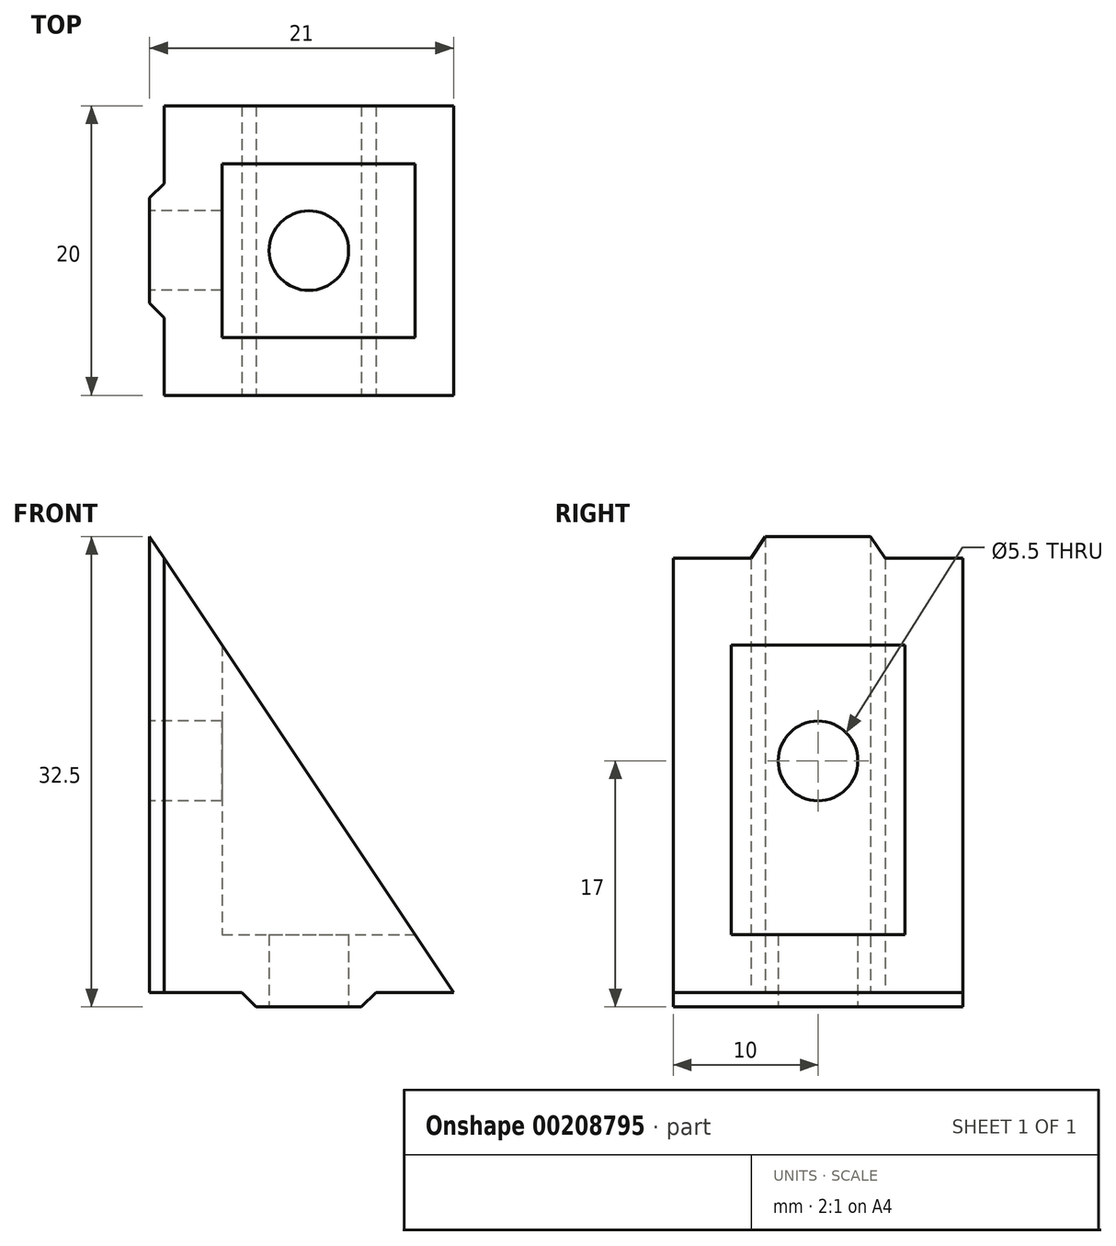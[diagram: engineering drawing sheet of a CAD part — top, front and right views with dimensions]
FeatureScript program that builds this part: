
annotation { "Feature Type Name" : "Feature", "Feature Type Description" : "" }
export const myFeature = defineFeature(function(context is Context, id is Id, definition is map)
    precondition{}
    {
        {
            var Q0;
            Q0=qCreatedBy(makeId("Top.planeOp"),FACE);
            var sketch = newSketch(context, id + "F0", { "sketchPlane" : qUnion([Q0])});
            skLineSegment(sketch, "E0.bottom", {"start": v(-20, 20) * mm, "end": v(0, 20) * mm});
            skLineSegment(sketch, "E0.top", {"start": v(-20, 0) * mm, "end": v(0, 0) * mm});
            skLineSegment(sketch, "E0.left", {"start": v(-20, 20) * mm, "end": v(-20, 0) * mm});
            skLineSegment(sketch, "E0.right", {"start": v(0, 20) * mm, "end": v(0, 0) * mm});
            skSolve(sketch);
        }
        {
            var Q0;
            Q0=makeQuery(id+"F0.imprint","IMPRINT",FACE,{"disambiguationData":[TD([[makeQuery(id+"F0.imprint","IMPRINT",EDGE,{"derivedFrom":sQuery(id+"F0.wireOp",EDGE,"E0.bottom")}),-1.0]])]});
            extrude(context, id + "F1", {"entities" : qUnion([Q0]), "depth" : 4 * mm});
        }
        {
            var Q0;
            Q0=makeQuery(id+"F1.opExtrude","CAP_FACE",FACE,{"disambiguationData":[OSD([sQuery(id+"F0.wireOp",EDGE,"E0.bottom"),sQuery(id+"F0.wireOp",EDGE,"E0.top"),sQuery(id+"F0.wireOp",EDGE,"E0.left"),sQuery(id+"F0.wireOp",EDGE,"E0.right")])],"isStart":false});
            var sketch = newSketch(context, id + "F2", { "sketchPlane" : qUnion([Q0])});
            skLineSegment(sketch, "E1", {"start": v(0, 0) * mm, "end": v(-20, 0) * mm});
            skLineSegment(sketch, "E2", {"start": v(-20, 0) * mm, "end": v(-20, 20) * mm});
            skLineSegment(sketch, "E3", {"start": v(-20, 20) * mm, "end": v(0, 20) * mm});
            skLineSegment(sketch, "E4", {"start": v(0, 20) * mm, "end": v(0, 16) * mm});
            skLineSegment(sketch, "E5", {"start": v(0, 16) * mm, "end": v(-16, 16) * mm});
            skLineSegment(sketch, "E6", {"start": v(-16, 16) * mm, "end": v(-16, 4) * mm});
            skLineSegment(sketch, "E7", {"start": v(-16, 4) * mm, "end": v(0, 4) * mm});
            skLineSegment(sketch, "E8", {"start": v(0, 4) * mm, "end": v(0, 0) * mm});
            skSolve(sketch);
        }
        {
            var Q0;
            Q0=makeQuery(id+"F2.imprint","IMPRINT",FACE,{"disambiguationData":[TD([[makeQuery(id+"F2.imprint","IMPRINT",EDGE,{"derivedFrom":sQuery(id+"F2.wireOp",EDGE,"E1")}),1.0]])]});
            extrude(context, id + "F3", {"entities" : qUnion([Q0]), "operationType" : NewBodyOperationType.ADD, "depth" : 26 * mm});
        }
        {
            var Q0;
            Q0=makeQuery(id+"F3.boolean.opBoolean","MERGE",FACE,{"derivedFrom":[makeQuery(id+"F1.opExtrude","SWEPT_FACE",FACE,{"disambiguationData":[OSD([sQuery(id+"F0.wireOp",EDGE,"E0.top")])]}),makeQuery(id+"F3.opExtrude","SWEPT_FACE",FACE,{"disambiguationData":[OSD([sQuery(id+"F2.wireOp",EDGE,"E1")])]})]});
            var sketch = newSketch(context, id + "F4", { "sketchPlane" : qUnion([Q0])});
            skLineSegment(sketch, "E9", {"start": v(-20, 30) * mm, "end": v(0, 30) * mm});
            skLineSegment(sketch, "E10", {"start": v(0, 30) * mm, "end": v(0, 0) * mm});
            skLineSegment(sketch, "E11", {"start": v(0, 0) * mm, "end": v(-20, 30) * mm});
            skSolve(sketch);
        }
        {
            var Q0;
            Q0=makeQuery(id+"F4.imprint","IMPRINT",FACE,{"disambiguationData":[TD([[makeQuery(id+"F4.imprint","IMPRINT",EDGE,{"derivedFrom":sQuery(id+"F4.wireOp",EDGE,"E9")}),-1.0]])]});
            extrude(context, id + "F5", {"entities" : qUnion([Q0]), "operationType" : NewBodyOperationType.REMOVE, "endBound" : BoundingType.THROUGH_ALL, "oppositeDirection" : true, "depth" : 25 * mm});
        }
        {
            var Q0;
            {var subQ0=sQuery(id+"F2.wireOp",EDGE,"E5");Q0=makeQuery(id+"F2.imprint","IMPRINT",FACE,{"disambiguationData":[TD([[makeQuery(id+"F2.imprint","IMPRINT",EDGE,{"derivedFrom":subQ0}),1.0]])]});}
            var sketch = newSketch(context, id + "F6", { "sketchPlane" : qUnion([Q0])});
            skLineSegment(sketch, "E12", {"start": v(-10, 4) * mm, "end": v(-10, 10) * mm});
            skLineSegment(sketch, "E13", {"start": v(-10, 10) * mm, "end": v(-10, 16) * mm});
            skSolve(sketch);
        }
        {
            var Q0;
            Q0=makeQuery(id+"F3.opExtrude","SWEPT_FACE",FACE,{"disambiguationData":[OSD([sQuery(id+"F2.wireOp",EDGE,"E6")])]});
            var sketch = newSketch(context, id + "F7", { "sketchPlane" : qUnion([Q0])});
            skLineSegment(sketch, "E14", {"start": v(16, 16) * mm, "end": v(10, 16) * mm});
            skLineSegment(sketch, "E15", {"start": v(10, 16) * mm, "end": v(4, 16) * mm});
            skLineSegment(sketch, "E16", {"start": v(10, 16) * mm, "end": v(10, 24) * mm});
            skSolve(sketch);
        }
        {
            var Q0;
            {var subQ0=sQuery(id+"F2.wireOp",EDGE,"E5");Q0=makeQuery(id+"F2.imprint","IMPRINT",FACE,{"disambiguationData":[TD([[makeQuery(id+"F2.imprint","IMPRINT",EDGE,{"derivedFrom":subQ0}),1.0]])]});}
            var sketch = newSketch(context, id + "F8", { "sketchPlane" : qUnion([Q0])});
            skLineSegment(sketch, "E17", {"start": v(-20, 0) * mm, "end": v(-20, 5.36) * mm, "construction": true});
            skLineSegment(sketch, "E18", {"start": v(-20, 5.36) * mm, "end": v(-20, 14.64) * mm});
            skLineSegment(sketch, "E19", {"start": v(-20, 14.64) * mm, "end": v(-20, 20) * mm, "construction": true});
            skLineSegment(sketch, "E20", {"start": v(-20, 14.64) * mm, "end": v(-21, 13.64) * mm});
            skLineSegment(sketch, "E21", {"start": v(-21, 13.64) * mm, "end": v(-21.8, 12.84) * mm, "construction": true});
            skLineSegment(sketch, "E22", {"start": v(-21.8, 12.84) * mm, "end": v(-24.64, 10) * mm, "construction": true});
            skLineSegment(sketch, "E23", {"start": v(-24.64, 10) * mm, "end": v(-21.8, 7.16) * mm, "construction": true});
            skLineSegment(sketch, "E24", {"start": v(-21.8, 7.16) * mm, "end": v(-21, 6.36) * mm, "construction": true});
            skLineSegment(sketch, "E25", {"start": v(-21, 6.36) * mm, "end": v(-20, 5.36) * mm});
            skLineSegment(sketch, "E26", {"start": v(-21, 6.36) * mm, "end": v(-21, 13.64) * mm});
            skLineSegment(sketch, "E27", {"start": v(-21.8, 12.84) * mm, "end": v(-21.8, 7.16) * mm, "construction": true});
            skLineSegment(sketch, "E28", {"start": v(-21, 10) * mm, "end": v(-20, 10) * mm, "construction": true});
            skSolve(sketch);
        }
        {
            var Q0;
            Q0=makeQuery(id+"F8.imprint","IMPRINT",FACE,{"disambiguationData":[TD([[makeQuery(id+"F8.imprint","IMPRINT",EDGE,{"derivedFrom":sQuery(id+"F8.wireOp",EDGE,"E18")}),1.0]])]});
            var Q1;
            Q1=sQuery(id+"F8.wireOp",EDGE,"E28");
            var Q2;
            Q2=sQuery(id+"F8.wireOp",EDGE,"E24");
            var Q3;
            Q3=sQuery(id+"F8.wireOp",EDGE,"E27");
            var Q4;
            Q4=sQuery(id+"F8.wireOp",EDGE,"E23");
            var Q5;
            Q5=sQuery(id+"F8.wireOp",EDGE,"E22");
            var Q6;
            Q6=sQuery(id+"F8.wireOp",EDGE,"E21");
            var Q7;
            Q7=sQuery(id+"F8.wireOp",EDGE,"E19");
            var Q8;
            Q8=sQuery(id+"F8.wireOp",EDGE,"E17");
            var Q9;
            Q9=makeQuery(id+"F5.boolean.opBoolean","COPY",FACE,{"derivedFrom":makeQuery(id+"F5.opExtrude","SWEPT_FACE",FACE,{"disambiguationData":[OSD([sQuery(id+"F4.wireOp",EDGE,"E11")])]})});
            var Q10;
            Q10=makeQuery(id+"F1.opExtrude","SWEPT_BODY",BODY,{"disambiguationData":[OSD([sQuery(id+"F0.wireOp",EDGE,"E0.bottom"),sQuery(id+"F0.wireOp",EDGE,"E0.top"),sQuery(id+"F0.wireOp",EDGE,"E0.left"),sQuery(id+"F0.wireOp",EDGE,"E0.right")])]});
            var Q11;
            Q11=makeQuery(id+"F1.opExtrude","CAP_FACE",FACE,{"disambiguationData":[OSD([sQuery(id+"F0.wireOp",EDGE,"E0.bottom"),sQuery(id+"F0.wireOp",EDGE,"E0.top"),sQuery(id+"F0.wireOp",EDGE,"E0.left"),sQuery(id+"F0.wireOp",EDGE,"E0.right")])],"isStart":true});
            extrude(context, id + "F9", {"entities" : qUnion([Q0]), "operationType" : NewBodyOperationType.ADD, "surfaceEntities" : qUnion([Q1, Q2, Q3, Q4, Q5, Q6, Q7, Q8]), "endBound" : BoundingType.UP_TO_SURFACE, "endBoundEntityFace" : qUnion([Q9]), "endBoundEntityBody" : qUnion([Q10]), "depth" : 25 * mm, "hasSecondDirection" : true, "secondDirectionBound" : BoundingType.UP_TO_SURFACE, "secondDirectionOppositeDirection" : true, "secondDirectionBoundEntityFace" : qUnion([Q11]), "secondDirectionDepth" : 25 * mm});
        }
        {
            var Q0;
            Q0=makeQuery(id+"F3.boolean.opBoolean","MERGE",FACE,{"derivedFrom":[makeQuery(id+"F1.opExtrude","SWEPT_FACE",FACE,{"disambiguationData":[OSD([sQuery(id+"F0.wireOp",EDGE,"E0.top")])]}),makeQuery(id+"F3.opExtrude","SWEPT_FACE",FACE,{"disambiguationData":[OSD([sQuery(id+"F2.wireOp",EDGE,"E1")])]})]});
            var sketch = newSketch(context, id + "F10", { "sketchPlane" : qUnion([Q0])});
            skLineSegment(sketch, "E29", {"start": v(0, 0) * mm, "end": v(-5.36, 0) * mm, "construction": true});
            skLineSegment(sketch, "E30", {"start": v(-5.36, 0) * mm, "end": v(-10, 0) * mm});
            skLineSegment(sketch, "E31", {"start": v(-10, 0) * mm, "end": v(-14.64, 0) * mm});
            skLineSegment(sketch, "E32", {"start": v(-14.64, 0) * mm, "end": v(-13.64, -1) * mm});
            skLineSegment(sketch, "E33", {"start": v(-13.64, -1) * mm, "end": v(-12.84, -1.8) * mm, "construction": true});
            skLineSegment(sketch, "E34", {"start": v(-12.84, -1.8) * mm, "end": v(-10, -4.64) * mm, "construction": true});
            skLineSegment(sketch, "E35", {"start": v(-10, -4.64) * mm, "end": v(-7.16, -1.8) * mm, "construction": true});
            skLineSegment(sketch, "E36", {"start": v(-7.16, -1.8) * mm, "end": v(-6.36, -1) * mm, "construction": true});
            skLineSegment(sketch, "E37", {"start": v(-6.36, -1) * mm, "end": v(-5.36, 0) * mm});
            skLineSegment(sketch, "E38", {"start": v(-7.16, -1.8) * mm, "end": v(-12.84, -1.8) * mm, "construction": true});
            skLineSegment(sketch, "E39", {"start": v(-6.36, -1) * mm, "end": v(-13.64, -1) * mm});
            skLineSegment(sketch, "E40", {"start": v(-10, -1) * mm, "end": v(-10, 0) * mm, "construction": true});
            skSolve(sketch);
        }
        {
            var Q0;
            Q0=qSketchRegion(id+"F10",true);
            var Q1;
            Q1=makeQuery(id+"F3.boolean.opBoolean","MERGE",FACE,{"derivedFrom":[makeQuery(id+"F1.opExtrude","SWEPT_FACE",FACE,{"disambiguationData":[OSD([sQuery(id+"F0.wireOp",EDGE,"E0.bottom")])]}),makeQuery(id+"F3.opExtrude","SWEPT_FACE",FACE,{"disambiguationData":[OSD([sQuery(id+"F2.wireOp",EDGE,"E3")])]})]});
            var Q2;
            Q2=makeQuery(id+"F1.opExtrude","SWEPT_BODY",BODY,{"disambiguationData":[OSD([sQuery(id+"F0.wireOp",EDGE,"E0.bottom"),sQuery(id+"F0.wireOp",EDGE,"E0.top"),sQuery(id+"F0.wireOp",EDGE,"E0.left"),sQuery(id+"F0.wireOp",EDGE,"E0.right")])]});
            extrude(context, id + "F11", {"entities" : qUnion([Q0]), "operationType" : NewBodyOperationType.ADD, "endBound" : BoundingType.UP_TO_SURFACE, "oppositeDirection" : true, "endBoundEntityFace" : qUnion([Q1]), "endBoundEntityBody" : qUnion([Q2]), "depth" : 25 * mm});
        }
        {
            var Q0;
            Q0=sQuery(id+"F6.wireOp",VERTEX,"E13.start");
            var Q1;
            Q1=sQuery(id+"F7.wireOp",VERTEX,"E16.start");
            var Q2;
            Q2=makeQuery(id+"F1.opExtrude","SWEPT_BODY",BODY,{"disambiguationData":[OSD([sQuery(id+"F0.wireOp",EDGE,"E0.bottom"),sQuery(id+"F0.wireOp",EDGE,"E0.top"),sQuery(id+"F0.wireOp",EDGE,"E0.left"),sQuery(id+"F0.wireOp",EDGE,"E0.right")])]});
            hole(context, id + "F12", {"style" : HoleStyle.SIMPLE, "endStyle" : HoleEndStyle.THROUGH, "standardTappedOrClearance" : lookupTablePath({ "standard" : "ISO", "fit" : "Normal", "size" : "M5", "type" : "Clearance" }), "standardBlindInLast" : lookupTablePath({ "fit" : "Standard", "standard" : "ISO", "size" : "M5", "type" : "Clearance" }), "holeDiameter" : 5.5 * mm, "locations" : qUnion([Q0, Q1]), "scope" : qUnion([Q2]), "isTappedThrough" : true});
        }
    });
